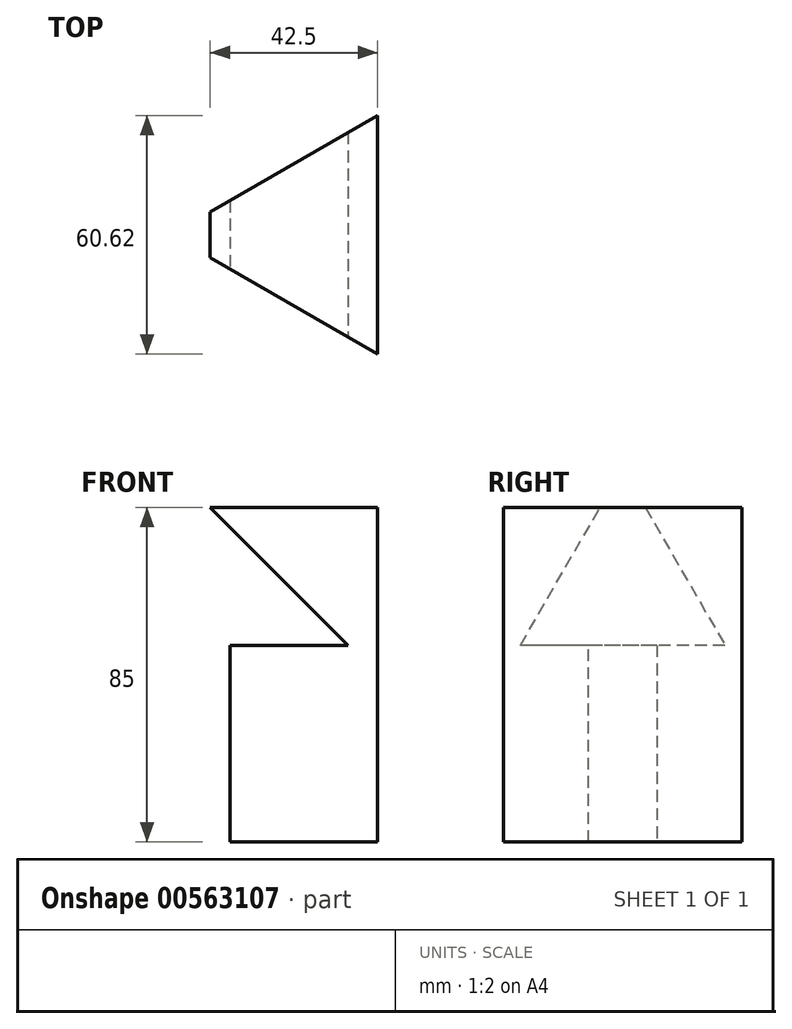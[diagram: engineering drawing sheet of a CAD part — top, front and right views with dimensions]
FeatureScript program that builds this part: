
annotation { "Feature Type Name" : "Feature", "Feature Type Description" : "" }
export const myFeature = defineFeature(function(context is Context, id is Id, definition is map)
    precondition{}
    {
        {
            var Q0;
            Q0=qCreatedBy(makeId("Top.planeOp"),FACE);
            var sketch = newSketch(context, id + "F0", { "sketchPlane" : qUnion([Q0])});
            skLineSegment(sketch, "E0", {"start": v(-35, 0) * mm, "end": v(17.5, 30.31) * mm});
            skLineSegment(sketch, "E1", {"start": v(17.5, 30.31) * mm, "end": v(17.5, -30.31) * mm});
            skLineSegment(sketch, "E2", {"start": v(17.5, -30.31) * mm, "end": v(-35, 0) * mm});
            skSolve(sketch);
        }
        {
            var Q0;
            Q0=makeQuery(id+"F0.imprint","IMPRINT",FACE,{"disambiguationData":[TD([[makeQuery(id+"F0.imprint","IMPRINT",EDGE,{"derivedFrom":sQuery(id+"F0.wireOp",EDGE,"E0")}),-1.0]])]});
            extrude(context, id + "F1", {"entities" : qUnion([Q0]), "depth" : 85 * mm, "offsetDistance" : 25 * mm});
        }
        {
            var Q0;
            Q0=qCreatedBy(makeId("Front.planeOp"),FACE);
            cPlane(context, id + "F2", {"entities" : qUnion([Q0]), "cplaneType" : CPlaneType.OFFSET, "offset" : 70 * mm, "width" : 150 * mm, "height" : 150 * mm});
        }
        {
            var Q0;
            Q0=qCreatedBy(id+"F2.planeOp",FACE);
            var sketch = newSketch(context, id + "F3", { "sketchPlane" : qUnion([Q0])});
            skLineSegment(sketch, "E3", {"start": v(-20, 0) * mm, "end": v(-20, 50) * mm});
            skLineSegment(sketch, "E4", {"start": v(-20, 50) * mm, "end": v(10, 50) * mm});
            skLineSegment(sketch, "E5", {"start": v(10, 50) * mm, "end": v(-25.16, 85.16) * mm});
            skLineSegment(sketch, "E6", {"start": v(-25.16, 85.16) * mm, "end": v(-42.8, 85.16) * mm});
            skLineSegment(sketch, "E7", {"start": v(-42.8, 85.16) * mm, "end": v(-44.77, 0) * mm});
            skLineSegment(sketch, "E8", {"start": v(-44.77, 0) * mm, "end": v(-20, 0) * mm});
            skSolve(sketch);
        }
        {
            var Q0;
            Q0=makeQuery(id+"F3.imprint","IMPRINT",FACE,{"disambiguationData":[TD([[makeQuery(id+"F3.imprint","IMPRINT",EDGE,{"derivedFrom":sQuery(id+"F3.wireOp",EDGE,"E3")}),1.0]])]});
            extrude(context, id + "F4", {"entities" : qUnion([Q0]), "operationType" : NewBodyOperationType.REMOVE, "oppositeDirection" : true, "depth" : 120 * mm, "offsetDistance" : 25 * mm});
        }
    });
